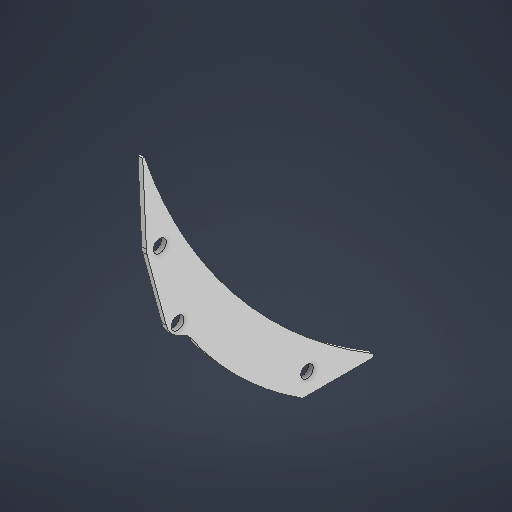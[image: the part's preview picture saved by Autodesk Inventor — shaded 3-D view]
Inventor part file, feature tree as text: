
AUTODESK INVENTOR PART (.ipt)
format: ipt  version: 2025.2 (Build 292293000, 293)  size: 207,872 bytes
history: native  units: in
note: dims shown in document units (in); Inventor stores cm internally (conversion verified against a paired STEP export)
features: extrude x1, sketch x1
ambient origin geometry x8: Origin, YZ Plane, XZ Plane, XY Plane, X Axis, Y Axis, Z Axis, Center Point
bodies: Solid1 (feature_tree)
feature tree (2):
  extrude  "Extrusion1"  Depth=0.0125in
  sketch  "Sketch1"  dims[d1=0.165in d4=1.0in d5=0.025in d6=0.0625in d7=0.0in d9=7.0in d10=0.172in d11=0.0125in]
